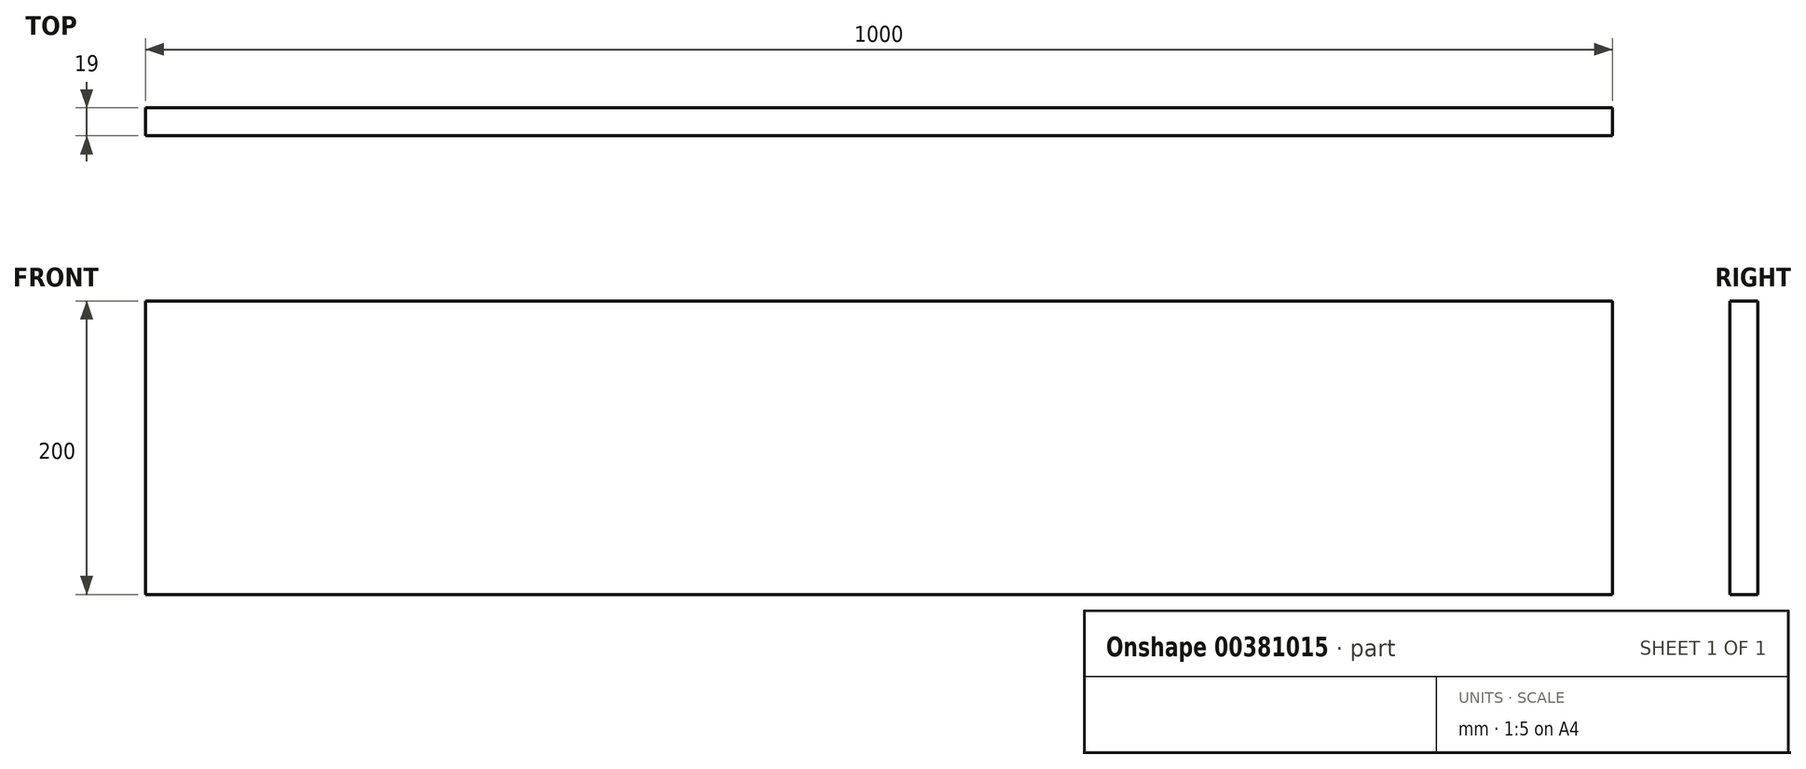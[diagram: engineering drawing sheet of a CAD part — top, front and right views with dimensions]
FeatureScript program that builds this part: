
annotation { "Feature Type Name" : "Feature", "Feature Type Description" : "" }
export const myFeature = defineFeature(function(context is Context, id is Id, definition is map)
    precondition{}
    {
        {
            var Q0;
            Q0=qCreatedBy(makeId("Front.planeOp"),FACE);
            var sketch = newSketch(context, id + "F0", { "sketchPlane" : qUnion([Q0])});
            skLineSegment(sketch, "E0.bottom", {"start": v(500, 100) * mm, "end": v(-500, 100) * mm});
            skLineSegment(sketch, "E0.top", {"start": v(500, -100) * mm, "end": v(-500, -100) * mm});
            skLineSegment(sketch, "E0.left", {"start": v(500, 100) * mm, "end": v(500, -100) * mm});
            skLineSegment(sketch, "E0.right", {"start": v(-500, 100) * mm, "end": v(-500, -100) * mm});
            skPoint(sketch, "E0.middle", {"position": v(0, 0) * mm});
            skSolve(sketch);
        }
        {
            var Q0;
            Q0=makeQuery(id+"F0.imprint","IMPRINT",FACE,{"disambiguationData":[TD([[makeQuery(id+"F0.imprint","IMPRINT",EDGE,{"derivedFrom":sQuery(id+"F0.wireOp",EDGE,"E0.bottom")}),1.0]])]});
            extrude(context, id + "F1", {"entities" : qUnion([Q0]), "depth" : 19 * mm});
        }
    });
